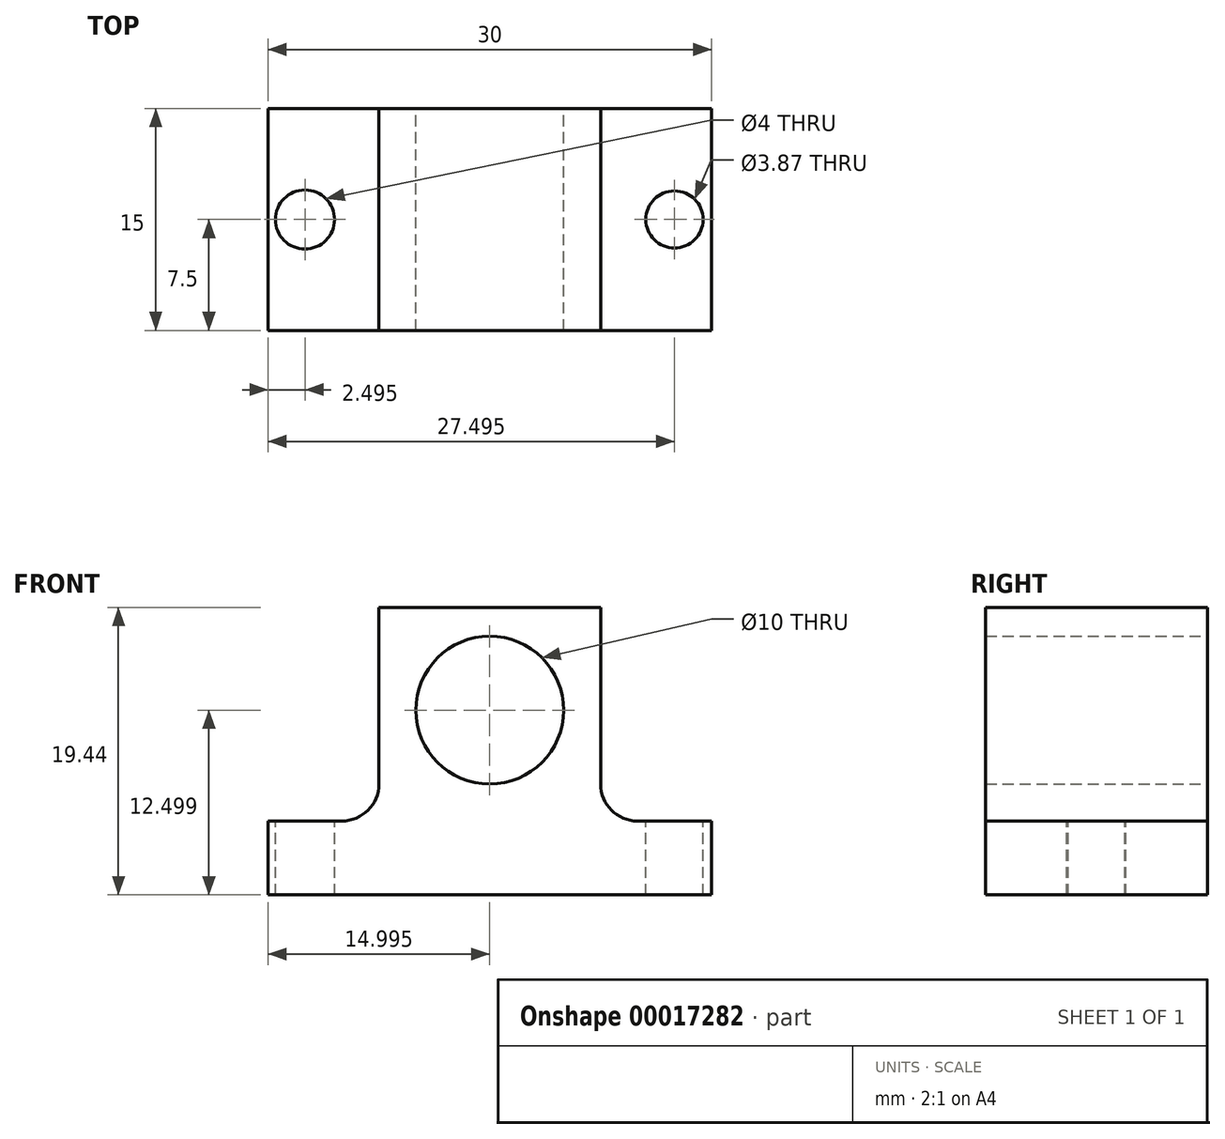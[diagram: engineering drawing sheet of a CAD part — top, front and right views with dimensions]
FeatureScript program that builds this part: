
annotation { "Feature Type Name" : "Feature", "Feature Type Description" : "" }
export const myFeature = defineFeature(function(context is Context, id is Id, definition is map)
    precondition{}
    {
        {
            var Q0;
            Q0=qCreatedBy(makeId("Front.planeOp"),FACE);
            var sketch = newSketch(context, id + "F0", { "sketchPlane" : qUnion([Q0])});
            skLineSegment(sketch, "E0", {"start": v(-48.3, 0.5) * mm, "end": v(-48.3, 5.5) * mm});
            skLineSegment(sketch, "E1", {"start": v(-48.3, 5.5) * mm, "end": v(-43.3, 5.5) * mm});
            skLineSegment(sketch, "E2", {"start": v(-40.8, 8) * mm, "end": v(-40.8, 19.95) * mm});
            skLineSegment(sketch, "E3", {"start": v(-40.8, 19.95) * mm, "end": v(-25.8, 19.95) * mm});
            skLineSegment(sketch, "E4", {"start": v(-25.8, 19.95) * mm, "end": v(-25.8, 8) * mm});
            skLineSegment(sketch, "E5", {"start": v(-23.3, 5.5) * mm, "end": v(-18.3, 5.5) * mm});
            skLineSegment(sketch, "E6", {"start": v(-18.3, 5.5) * mm, "end": v(-18.3, 0.5) * mm});
            skLineSegment(sketch, "E7", {"start": v(-48.3, 0.5) * mm, "end": v(-18.3, 0.5) * mm});
            skPoint(sketch, "E8.visualSharp", {"position": v(-40.8, 5.5) * mm});
            skArc(sketch, "E8.filletArc", {"start": v(-43.3, 5.5) * mm, "mid": v(-41.53, 6.24) * mm, "end": v(-40.8, 8) * mm});
            skPoint(sketch, "E9.visualSharp", {"position": v(-25.8, 5.5) * mm});
            skArc(sketch, "E9.filletArc", {"start": v(-25.8, 8) * mm, "mid": v(-25.06, 6.24) * mm, "end": v(-23.3, 5.5) * mm});
            skCircle(sketch, "E10", {"center": v(-33.3, 13) * mm, "radius": 5 * mm});
            skSolve(sketch);
        }
        {
            var Q0;
            Q0=makeQuery(id+"F0.imprint","IMPRINT",FACE,{"disambiguationData":[TD([[makeQuery(id+"F0.imprint","IMPRINT",EDGE,{"derivedFrom":sQuery(id+"F0.wireOp",EDGE,"E0")}),-1.0]])]});
            extrude(context, id + "F1", {"entities" : qUnion([Q0]), "depth" : 15 * mm});
        }
        {
            var Q0;
            Q0=makeQuery(id+"F1.opExtrude","SWEPT_FACE",FACE,{"disambiguationData":[OSD([sQuery(id+"F0.wireOp",EDGE,"E1")])]});
            var sketch = newSketch(context, id + "F2", { "sketchPlane" : qUnion([Q0])});
            skCircle(sketch, "E11", {"center": v(-45.8, -7.5) * mm, "radius": 2 * mm});
            skSolve(sketch);
        }
        {
            var Q0;
            Q0=makeQuery(id+"F1.opExtrude","SWEPT_FACE",FACE,{"disambiguationData":[OSD([sQuery(id+"F0.wireOp",EDGE,"E5")])]});
            var sketch = newSketch(context, id + "F3", { "sketchPlane" : qUnion([Q0])});
            skCircle(sketch, "E12", {"center": v(-20.8, -7.5) * mm, "radius": 1.93 * mm});
            skSolve(sketch);
        }
        {
            var Q0;
            Q0=makeQuery(id+"F2.imprint","IMPRINT",FACE,{"disambiguationData":[TD([[makeQuery(id+"F2.imprint","IMPRINT",EDGE,{"derivedFrom":sQuery(id+"F2.wireOp",EDGE,"E11")}),1.0]])]});
            extrude(context, id + "F4", {"entities" : qUnion([Q0]), "operationType" : NewBodyOperationType.REMOVE, "oppositeDirection" : true, "depth" : 25 * mm});
        }
        {
            var Q0;
            Q0=makeQuery(id+"F3.imprint","IMPRINT",FACE,{"disambiguationData":[TD([[makeQuery(id+"F3.imprint","IMPRINT",EDGE,{"derivedFrom":sQuery(id+"F3.wireOp",EDGE,"E12")}),1.0]])]});
            extrude(context, id + "F5", {"entities" : qUnion([Q0]), "operationType" : NewBodyOperationType.REMOVE, "oppositeDirection" : true, "depth" : 25 * mm});
        }
    });
